# Revit family: URA NEXT Standard Export - Non Permanent-Wall Mounted
name_source: partatom
category: Luminaires
units: mm (PartAtom-declared; Revit-internal decimal feet)

## family parameters
Cote de connecteur circulaire = Utiliser le diamètre
Couper avec des vides une fois chargée = Non
Hôte = Face
Partagée = Non
Repere pour localisation dans la piece = Non
Source d'éclairage = Non
Type d'élément = Normal

## types (7) — shared parameters
Color = White
Connected Object = Non
Connection type = Screw connection
Control system = without
Elévation par défaut = 2300 mm
Emergency power supply = Autonomous (individual battery)
Fabricant = LEGRAND
Frequency = 50-60
Function = Escape and mood lighting
General Conditions of Use = https://export.legrand.com
Height = 40 mm  [stored 0.131234 ft]
Horizontal mounting distance = 80-90
IK = 07
IP = 42
Installation method = Surface mounting (wall_ceiling)
Length = 202 mm  [stored 0.66273 ft]
Material = Plastic
Operating temperature MIN-MAX = -5-35
Pictogram type = Sticker
Power supply = 230 AC/DC
Protection class = II
Standby consumption = 0.0 mA
Switching type = Non permanent
URL = https://www.legrand.com
Vertical mounting distance = 55-65
Width = 104 mm
battery status = NiCd
light source = LED not exchangeable
terminal capacity = 1.5-2.5
zero-valued in all types: Recessed height, Recessed length, Recessed width

## per-type parameters (varying)
| type | Autonomy | Product designation | Reference | Spare battery | System power | Useful luminous flux |
| 70LM-1H Wall Mount | 1H | EMERGENCY LIGHT X-LIGHT 180 SURFACE NON PERMANENT 70LM 1H STANDARD | LG-660051 | 660180 | 1 W | 70 lm |
| 100LM-1H Wall Mounted | 1H | EMERGENCY LIGHT X-LIGHT 180 SURFACE NON PERMANENT 100LM 1H STANDARD | LG-660052 | 660180 | 1 W | 100 lm |
| 100LM-1H Wall Installation-With Picto | 1H | EMERGENCY LIGHT X-LIGHT 180 SURFACE NON PERMANENT 100LM 1H STANDARD WITH  LABEL | LG-660053 | 660180 | 1 W | 100 lm |
| 200LM-1H Wall Mounted | 1H | EMERGENCY LIGHT X-LIGHT 180 SURFACE NON PERMANENT 200LM 1H STANDARD | LG-660054 | 660181 | 2 W | 200 lm |
| 200LM-2H Wall Mounted | 2H | EMERGENCY LIGHT X-LIGHT 180 SURFACE NON PERMANENT 200LM 2H STANDARD | LG-660057 | 660184 | 0 W | 200 lm |
| 100LM-3H Wall Mounted | 3H | EMERGENCY LIGHT X-LIGHT 180 SURFACE NON PERMANENT 100LM 3H STANDARD | LG-660059 | 660181 | 2 W | 100 lm |
| 100LM-3H Wall Installation-With Picto | 3H | EMERGENCY LIGHT X-LIGHT 180 SURFACE NON PERMANENT 100LM 3H STANDARD WITH LABEL | LG-660060 | 660181 | 2 W | 100 lm |

note: [stored X ft] marks values corroborated as IEEE doubles in the binary element streams (Revit-internal decimal feet)
